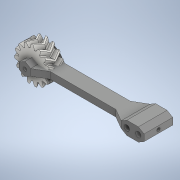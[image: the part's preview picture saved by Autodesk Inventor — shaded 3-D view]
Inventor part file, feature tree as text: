
AUTODESK INVENTOR PART (.ipt)
format: ipt  version: 2020 (Build 240168000, 168)  size: 985,600 bytes
history: native  units: in
note: dims shown in document units (in); Inventor stores cm internally (conversion verified against a paired STEP export)
features: sketch x5, extrude x4, other x3, plane x2, mirror x1, projected_geometry x1
ambient origin geometry x8: Origin, YZ Plane, XZ Plane, XY Plane, X Axis, Y Axis, Z Axis, Center Point
bodies: Solid1 (feature_tree), Solid2 (feature_tree)
feature tree (16):
  other  "Spur Gear1"
  plane  "Work Plane3"
  extrude  "Extrusion1"  Depth=3.4256in
  plane  "Work Plane1"
  extrude  "Extrusion2"  Depth=0.7874in
  sketch  "Sketch4"  dims[d4=0.0in d5=0.0906in]
  extrude  "Extrusion4"  Depth=0.0906in
  mirror  "Mirror3"
  extrude  "Extrusion11"  Depth=0.315in
  sketch  "Sketch1"  dims[d0=0.1818in d1=3.4256in]
  sketch  "Sketch2"  dims[d2=0.0945in d3=0.7874in]
  sketch  "Sketch5"  dims[d6=0.7874in d7=0.0in d29=0.315in]
  other  "Solid1::Spur Gear1"
  other  "TaggingFeature1"
  projected_geometry  "Projected Loop11"
  sketch  "Sketch15"  dims[d31=0.315in d33=0.1476in d34=0.2362in d35=0.0in d38=0.315in d69=2.4807in d70=0.3937in d71=0.1969in d79=0.0in d80=0.3937in d81=0.0in]
